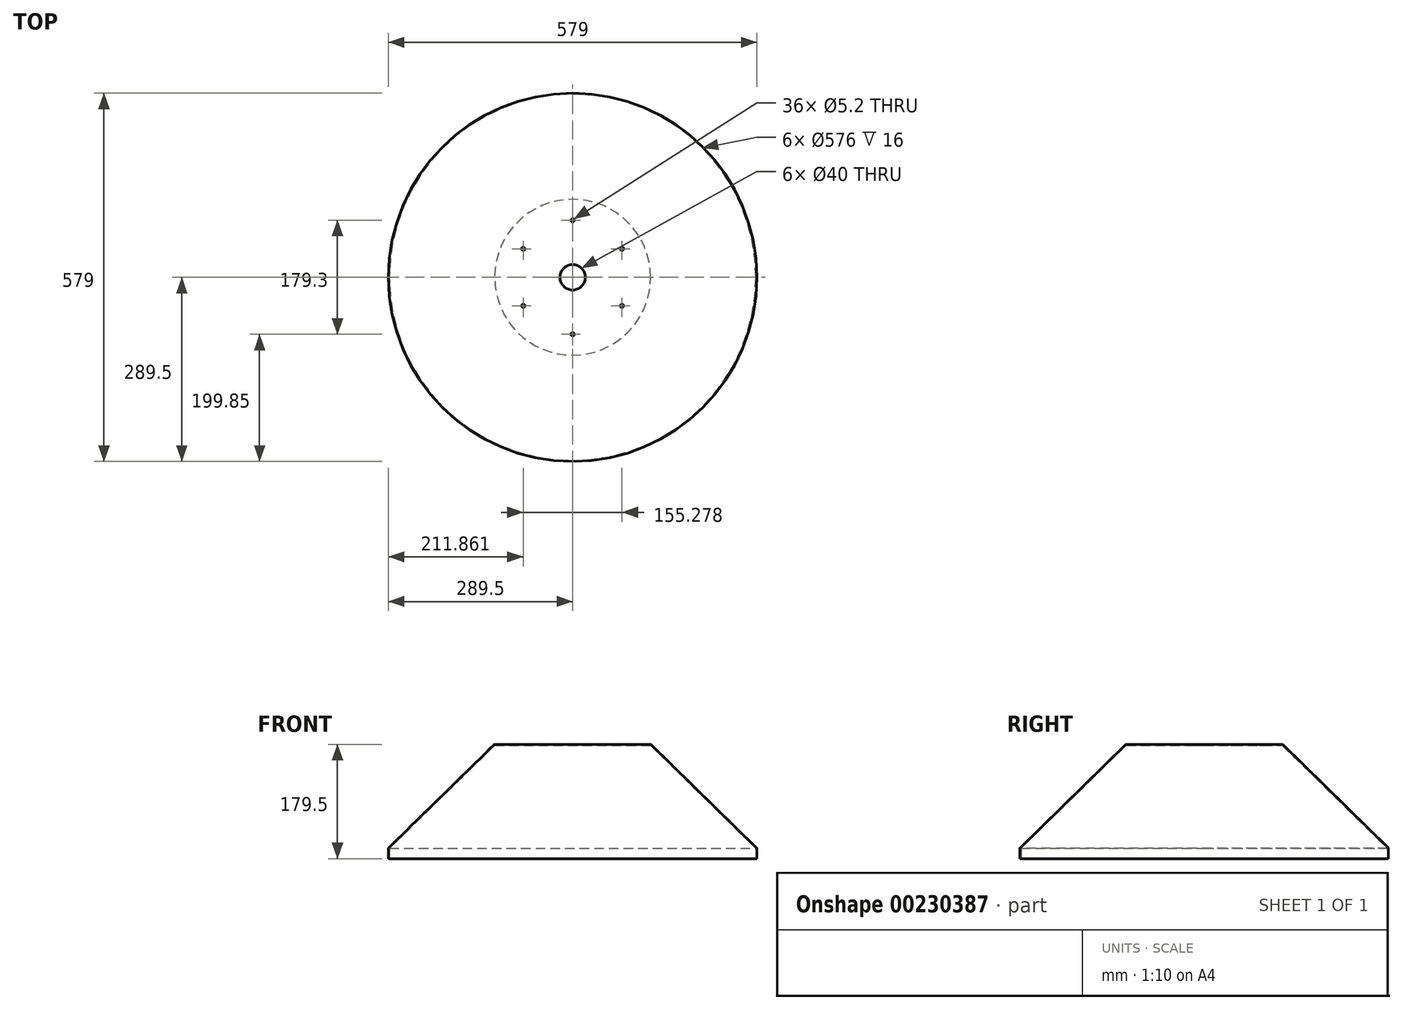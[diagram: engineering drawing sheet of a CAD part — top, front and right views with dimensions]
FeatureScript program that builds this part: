
annotation { "Feature Type Name" : "Feature", "Feature Type Description" : "" }
export const myFeature = defineFeature(function(context is Context, id is Id, definition is map)
    precondition{}
    {
        {
            var Q0;
            Q0=qCreatedBy(makeId("Front.planeOp"),FACE);
            var sketch = newSketch(context, id + "F0", { "sketchPlane" : qUnion([Q0])});
            skLineSegment(sketch, "E0", {"start": v(0, 0) * mm, "end": v(288, 0) * mm, "construction": true});
            skLineSegment(sketch, "E1", {"start": v(288, 0) * mm, "end": v(288, 16) * mm});
            skLineSegment(sketch, "E2", {"start": v(288, 16) * mm, "end": v(122.5, 178) * mm});
            skLineSegment(sketch, "E3.0", {"start": v(289.2, 16.92) * mm, "end": v(123.4, 179.21) * mm});
            skLineSegment(sketch, "E4.0", {"start": v(289.5, 0) * mm, "end": v(289.5, 16.21) * mm});
            skLineSegment(sketch, "E5", {"start": v(288, 0) * mm, "end": v(289.5, 0) * mm});
            skLineSegment(sketch, "E6", {"start": v(0, 0) * mm, "end": v(0, 178) * mm, "construction": true});
            skPoint(sketch, "E7.visualSharp", {"position": v(289.5, 16.63) * mm});
            skArc(sketch, "E7.filletArc", {"start": v(289.5, 16.21) * mm, "mid": v(289.42, 16.6) * mm, "end": v(289.2, 16.92) * mm});
            skLineSegment(sketch, "E8", {"start": v(122.5, 178) * mm, "end": v(0, 178) * mm});
            skLineSegment(sketch, "E9.0", {"start": v(122.7, 179.5) * mm, "end": v(0, 179.5) * mm});
            skPoint(sketch, "E10.visualSharp", {"position": v(123.11, 179.5) * mm});
            skArc(sketch, "E10.filletArc", {"start": v(123.4, 179.21) * mm, "mid": v(123.08, 179.43) * mm, "end": v(122.7, 179.5) * mm});
            skLineSegment(sketch, "E11", {"start": v(0, 179.5) * mm, "end": v(0, 178) * mm});
            skSolve(sketch);
        }
        {
            var Q0;
            Q0 = qSketchRegion(id + "F0", true);
            var Q1;
            Q1=sQuery(id+"F0.wireOp",EDGE,"E6");
            revolve(context, id + "F1", {"entities" : qUnion([Q0]), "axis" : qUnion([Q1]), "revolveType" : RevolveType.FULL});
        }
        {
            var Q0;
            Q0=makeQuery(id+"F1.opRevolve","SWEPT_FACE",FACE,{"disambiguationData":[OSD([sQuery(id+"F0.wireOp",EDGE,"E9.0")])]});
            var sketch = newSketch(context, id + "F2", { "sketchPlane" : qUnion([Q0])});
            skCircle(sketch, "E12.0", {"center": v(0, 0) * mm, "radius": 123 * mm, "construction": true});
            skCircle(sketch, "E13", {"center": v(0, 0) * mm, "radius": 5 * mm});
            skSolve(sketch);
        }
        {
            var Q0;
            Q0=qSketchRegion(id+"F2",true);
            extrude(context, id + "F3", {"entities" : qUnion([Q0]), "operationType" : NewBodyOperationType.REMOVE, "endBound" : BoundingType.UP_TO_NEXT, "oppositeDirection" : true, "depth" : 25 * mm});
        }
        {
            var Q0;
            Q0=makeQuery(id+"F1.opRevolve","SWEPT_FACE",FACE,{"disambiguationData":[OSD([sQuery(id+"F0.wireOp",EDGE,"E9.0")])]});
            var sketch = newSketch(context, id + "F4", { "sketchPlane" : qUnion([Q0])});
            skCircle(sketch, "E14", {"center": v(0, 0) * mm, "radius": 20 * mm});
            skSolve(sketch);
        }
        {
            var Q0;
            Q0=qSketchRegion(id+"F4",true);
            extrude(context, id + "F5", {"entities" : qUnion([Q0]), "operationType" : NewBodyOperationType.REMOVE, "endBound" : BoundingType.THROUGH_ALL, "oppositeDirection" : true, "depth" : 25 * mm});
        }
        {
            var Q0;
            Q0=makeQuery(id+"F1.opRevolve","SWEPT_FACE",FACE,{"disambiguationData":[OSD([sQuery(id+"F0.wireOp",EDGE,"E9.0")])]});
            var sketch = newSketch(context, id + "F6", { "sketchPlane" : qUnion([Q0])});
            skCircle(sketch, "E15", {"center": v(0, 0) * mm, "radius": 89.65 * mm, "construction": true});
            skCircle(sketch, "E16", {"center": v(0, 89.65) * mm, "radius": 2.6 * mm});
            skCircle(sketch, "E17.1.0", {"center": v(-77.64, 44.83) * mm, "radius": 2.6 * mm});
            skCircle(sketch, "E17.2.0", {"center": v(-77.64, -44.82) * mm, "radius": 2.6 * mm});
            skCircle(sketch, "E18.1.3.0", {"center": v(0, -89.65) * mm, "radius": 2.6 * mm});
            skCircle(sketch, "E18.1.4.0", {"center": v(77.64, -44.83) * mm, "radius": 2.6 * mm});
            skCircle(sketch, "E18.1.5.0", {"center": v(77.64, 44.83) * mm, "radius": 2.6 * mm});
            skSolve(sketch);
        }
        {
            var Q0;
            Q0 = qSketchRegion(id + "F6", true);
            extrude(context, id + "F7", {"entities" : qUnion([Q0]), "operationType" : NewBodyOperationType.REMOVE, "endBound" : BoundingType.THROUGH_ALL, "oppositeDirection" : true, "depth" : 25 * mm});
        }
    });
